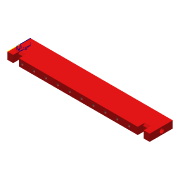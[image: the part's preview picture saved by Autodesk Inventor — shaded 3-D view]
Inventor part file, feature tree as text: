
AUTODESK INVENTOR PART (.ipt)
format: ipt  version: 2016 (Build 200138000, 138)  size: 264,704 bytes
history: native  units: mm
features: hole x5, sketch x5, extrude x2, pattern_linear x1, chamfer x1
ambient origin geometry x8: Origin, YZ Plane, XZ Plane, XY Plane, X Axis, Y Axis, Z Axis, Center Point
bodies: Volumenkörper1 (feature_tree)
feature tree (14):
  extrude  "Extrusion1"  Depth=240.0mm
  hole  "Bohrung7"  [1 undecoded]
  hole  "Bohrung8"  [1 undecoded]
  hole  "Bohrung9"  [1 undecoded]
  hole  "Bohrung10"  [1 undecoded]
  pattern_linear  "Rechteckige Anordnung3"  Spacing1=3.25mm  [1 undecoded]
  extrude  "Extrusion6"  Depth=10.0mm
  chamfer  "Fase2"  Distance=100.0mm
  hole  "Hole31"  [1 undecoded]
  sketch  "Skizze1"  dims[d0=39.0mm d1=240.0mm]
  sketch  "Skizze6"  dims[d2=12.0mm d3=0.0mm d77=25.0mm]
  sketch  "Skizze7"  dims[d79=18.8mm d80=13.8mm]
  sketch  "Skizze19"  dims[d81=1.2mm d82=6.0mm d83=4.0mm d84=2.0mm d85=90.0deg d86=6.0mm d87=20.594885mm d88=15.5mm]
  sketch  "Sketch21"  dims[d89=15.5mm d90=3.25mm d91=3.25mm d92=1.221mm d93=5.0mm d94=4.0mm d95=2.0mm d96=90.0deg d97=7.0mm d98=20.594885mm d99=6.0mm d100=25.0mm d101=2.0mm d102=5.0mm d103=4.0mm d104=2.0mm d105=90.0deg d106=14.0mm d107=20.594885mm d108=10.0mm d109=10.0mm d110=4.134mm d111=6.0mm d112=4.0mm d113=2.0mm d114=90.0deg d115=7.0mm d116=20.594885mm d117=100.0mm d119=20.0mm d312=10.0mm d313=0.0mm d314=3.0mm d315=2.0mm d316=45.0deg d319=10.0mm d320=10.0mm d321=9.0mm d341=6.0mm d342=18.0mm d343=8.0mm d344=8.0mm d345=6.0mm d346=4.0mm d347=2.0mm d348=90.0deg d349=220.0mm d350=20.594885mm]
note: 6 required parameter values undecoded (feature->parameter linkage not recoverable at this tier; creation-order binding heuristic only, values carry confidence <= 0.55)
